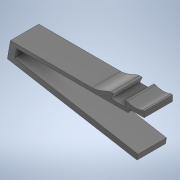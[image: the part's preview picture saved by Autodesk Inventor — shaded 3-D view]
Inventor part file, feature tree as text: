
AUTODESK INVENTOR PART (.ipt)
format: ipt  version: 2020 (Build 240168000, 168)  size: 155,648 bytes
history: native  units: mm
features: other x1, extrude x1, sketch x1
ambient origin geometry x8: Origin, YZ Plane, XZ Plane, XY Plane, X Axis, Y Axis, Z Axis, Center Point
bodies: Body1 (feature_tree)
feature tree (3):
  other  "Твердое тело1"
  extrude  "Выдавливание1"  Depth=10.0mm
  sketch  "Эскиз1"
